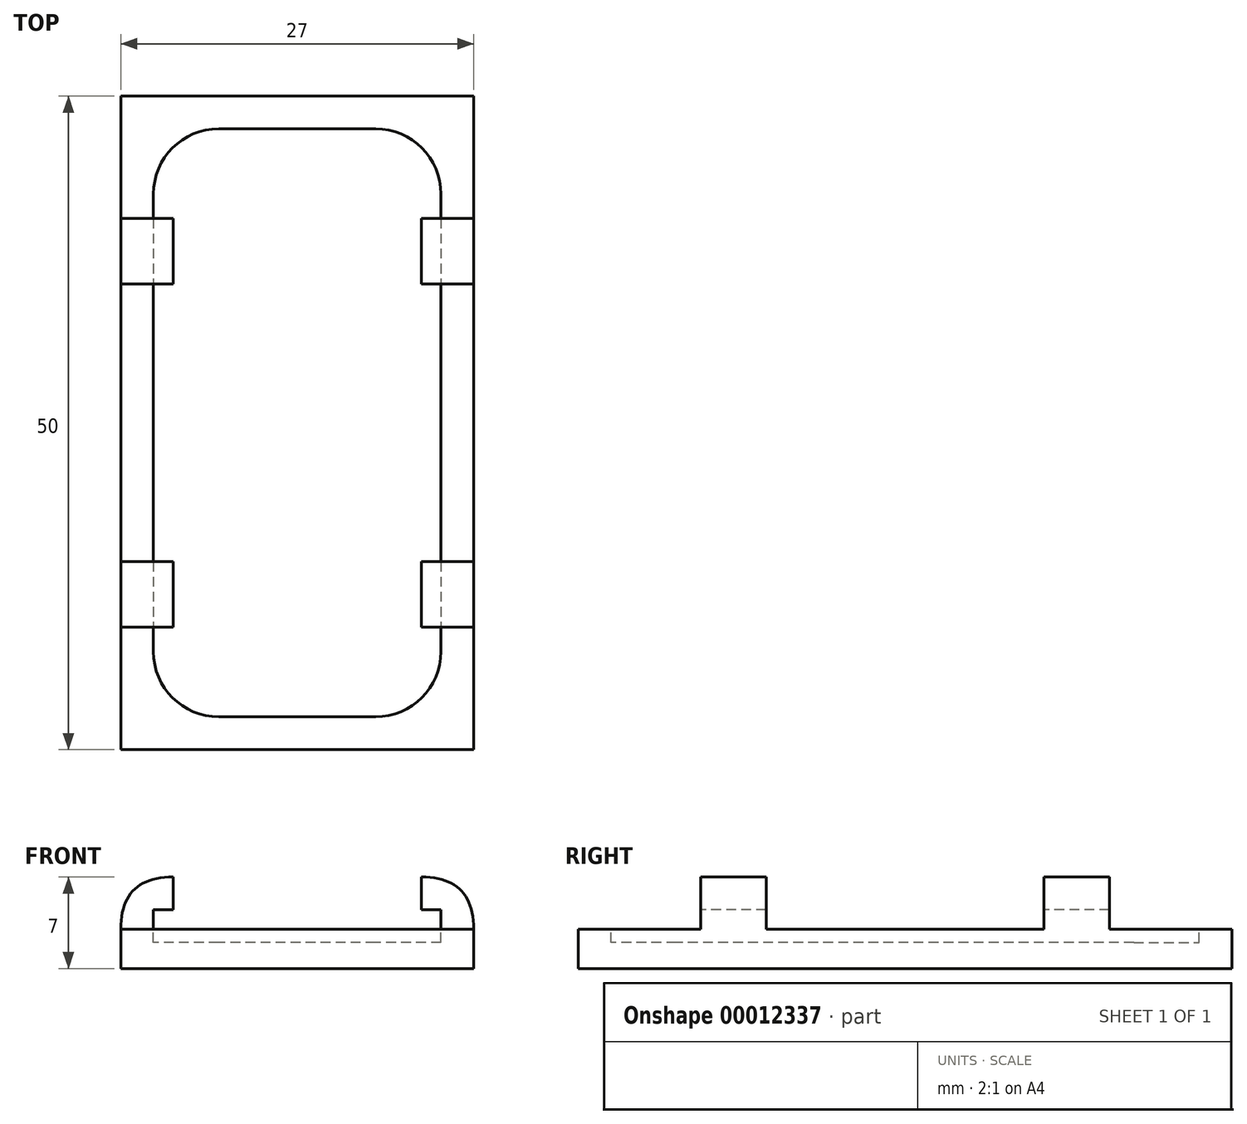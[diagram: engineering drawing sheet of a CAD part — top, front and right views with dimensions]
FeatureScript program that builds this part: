
annotation { "Feature Type Name" : "Feature", "Feature Type Description" : "" }
export const myFeature = defineFeature(function(context is Context, id is Id, definition is map)
    precondition{}
    {
        {
            var Q0;
            Q0=qCreatedBy(makeId("Top.planeOp"),FACE);
            var sketch = newSketch(context, id + "F0", { "sketchPlane" : qUnion([Q0])});
            skLineSegment(sketch, "E0.rect.bottom", {"start": v(13.5, 25) * mm, "end": v(-13.5, 25) * mm});
            skLineSegment(sketch, "E0.rect.top", {"start": v(13.5, -25) * mm, "end": v(-13.5, -25) * mm});
            skLineSegment(sketch, "E0.rect.left", {"start": v(13.5, 25) * mm, "end": v(13.5, -25) * mm});
            skLineSegment(sketch, "E0.rect.right", {"start": v(-13.5, 25) * mm, "end": v(-13.5, -25) * mm});
            skPoint(sketch, "E0.rect.middle", {"position": v(0, 0) * mm});
            skSolve(sketch);
        }
        {
            var Q0;
            Q0=qSketchRegion(id+"F0",true);
            extrude(context, id + "F1", {"entities" : qUnion([Q0]), "depth" : 3 * mm});
        }
        {
            var Q0;
            Q0=makeQuery(id+"F1.opExtrude","CAP_FACE",FACE,{"disambiguationData":[OSD([sQuery(id+"F0.wireOp",EDGE,"E0.rect.bottom"),sQuery(id+"F0.wireOp",EDGE,"E0.rect.top"),sQuery(id+"F0.wireOp",EDGE,"E0.rect.left"),sQuery(id+"F0.wireOp",EDGE,"E0.rect.right")])],"isStart":false});
            var sketch = newSketch(context, id + "F2", { "sketchPlane" : qUnion([Q0])});
            skLineSegment(sketch, "E1", {"start": v(-74.9, 0) * mm, "end": v(74.9, 0) * mm, "construction": true});
            skLineSegment(sketch, "E2", {"start": v(0, 55.47) * mm, "end": v(0, -72.68) * mm, "construction": true});
            skLineSegment(sketch, "E3.bottom", {"start": v(-13.5, 15.63) * mm, "end": v(-9.5, 15.63) * mm});
            skLineSegment(sketch, "E3.top", {"start": v(-13.5, 10.63) * mm, "end": v(-9.5, 10.63) * mm});
            skLineSegment(sketch, "E3.left", {"start": v(-13.5, 15.63) * mm, "end": v(-13.5, 10.63) * mm});
            skLineSegment(sketch, "E3.right", {"start": v(-9.5, 15.63) * mm, "end": v(-9.5, 10.63) * mm});
            skLineSegment(sketch, "E4.0.MirrorCS", {"start": v(13.5, 15.63) * mm, "end": v(9.5, 15.63) * mm});
            skLineSegment(sketch, "E5.0.MirrorCS", {"start": v(9.5, 15.63) * mm, "end": v(9.5, 10.63) * mm});
            skLineSegment(sketch, "E6.0.MirrorCS", {"start": v(13.5, 10.63) * mm, "end": v(9.5, 10.63) * mm});
            skLineSegment(sketch, "E7.0.MirrorCS", {"start": v(13.5, 15.63) * mm, "end": v(13.5, 10.63) * mm});
            skLineSegment(sketch, "E8.0.MirrorCS", {"start": v(-13.5, -10.63) * mm, "end": v(-9.5, -10.63) * mm});
            skLineSegment(sketch, "E9.0.MirrorCS", {"start": v(-9.5, -15.63) * mm, "end": v(-9.5, -10.63) * mm});
            skLineSegment(sketch, "E10.0.MirrorCS", {"start": v(-13.5, -15.63) * mm, "end": v(-9.5, -15.63) * mm});
            skLineSegment(sketch, "E11.0.MirrorCS", {"start": v(-13.5, -15.63) * mm, "end": v(-13.5, -10.63) * mm});
            skLineSegment(sketch, "E12.0.MirrorCS", {"start": v(13.5, -10.63) * mm, "end": v(9.5, -10.63) * mm});
            skLineSegment(sketch, "E13.0.MirrorCS", {"start": v(9.5, -15.63) * mm, "end": v(9.5, -10.63) * mm});
            skLineSegment(sketch, "E14.0.MirrorCS", {"start": v(13.5, -15.63) * mm, "end": v(9.5, -15.63) * mm});
            skLineSegment(sketch, "E15.0.MirrorCS", {"start": v(13.5, -15.63) * mm, "end": v(13.5, -10.63) * mm});
            skSolve(sketch);
        }
        {
            var Q0;
            Q0=makeQuery(id+"F2.imprint","IMPRINT",FACE,{"disambiguationData":[TD([[makeQuery(id+"F2.imprint","IMPRINT",EDGE,{"derivedFrom":makeQuery(id+"F1.opExtrude","CAP_EDGE",EDGE,{"disambiguationData":[OSD([sQuery(id+"F0.wireOp",EDGE,"E0.rect.bottom")])],"isStart":false})}),1.0]])]});
            var sketch = newSketch(context, id + "F3", { "sketchPlane" : qUnion([Q0])});
            skLineSegment(sketch, "E16.0", {"start": v(6, 22.5) * mm, "end": v(-6, 22.5) * mm});
            skLineSegment(sketch, "E16.1", {"start": v(11, 17.5) * mm, "end": v(11, -17.5) * mm});
            skLineSegment(sketch, "E16.2", {"start": v(6, -22.5) * mm, "end": v(-6, -22.5) * mm});
            skLineSegment(sketch, "E16.3", {"start": v(-11, 17.5) * mm, "end": v(-11, -17.5) * mm});
            skPoint(sketch, "E17.visualSharp", {"position": v(-11, 22.5) * mm});
            skArc(sketch, "E17.filletArc", {"start": v(-6, 22.5) * mm, "mid": v(-9.54, 21.04) * mm, "end": v(-11, 17.5) * mm});
            skPoint(sketch, "E18.visualSharp", {"position": v(11, 22.5) * mm});
            skArc(sketch, "E18.filletArc", {"start": v(11, 17.5) * mm, "mid": v(9.54, 21.04) * mm, "end": v(6, 22.5) * mm});
            skPoint(sketch, "E19.visualSharp", {"position": v(11, -22.5) * mm});
            skArc(sketch, "E19.filletArc", {"start": v(6, -22.5) * mm, "mid": v(9.54, -21.04) * mm, "end": v(11, -17.5) * mm});
            skPoint(sketch, "E20.visualSharp", {"position": v(-11, -22.5) * mm});
            skArc(sketch, "E20.filletArc", {"start": v(-11, -17.5) * mm, "mid": v(-9.54, -21.04) * mm, "end": v(-6, -22.5) * mm});
            skSolve(sketch);
        }
        {
            var Q0;
            Q0=qSketchRegion(id+"F3",true);
            extrude(context, id + "F4", {"entities" : qUnion([Q0]), "operationType" : NewBodyOperationType.REMOVE, "oppositeDirection" : true, "depth" : 1 * mm});
        }
        {
            var Q0;
            Q0=qSketchRegion(id+"F2",true);
            extrude(context, id + "F5", {"entities" : qUnion([Q0]), "operationType" : NewBodyOperationType.ADD, "depth" : 4 * mm});
        }
        {
            var Q0;
            Q0=makeQuery(id+"F5.opExtrude","SWEPT_FACE",FACE,{"disambiguationData":[OSD([sQuery(id+"F2.wireOp",EDGE,"E10.0.MirrorCS")])]});
            var sketch = newSketch(context, id + "F6", { "sketchPlane" : qUnion([Q0])});
            skLineSegment(sketch, "E21.bottom", {"start": v(-9.5, 4.5) * mm, "end": v(-11, 4.5) * mm});
            skLineSegment(sketch, "E21.top", {"start": v(-9.5, 3) * mm, "end": v(-11, 3) * mm});
            skLineSegment(sketch, "E21.left", {"start": v(-9.5, 4.5) * mm, "end": v(-9.5, 3) * mm});
            skLineSegment(sketch, "E21.right", {"start": v(-11, 4.5) * mm, "end": v(-11, 3) * mm});
            skLineSegment(sketch, "E22.0.MirrorCS", {"start": v(11, 4.5) * mm, "end": v(11, 3) * mm});
            skLineSegment(sketch, "E23.0.MirrorCS", {"start": v(9.5, 4.5) * mm, "end": v(11, 4.5) * mm});
            skLineSegment(sketch, "E24.0.MirrorCS", {"start": v(9.5, 4.5) * mm, "end": v(9.5, 3) * mm});
            skLineSegment(sketch, "E25.0.MirrorCS", {"start": v(9.5, 3) * mm, "end": v(11, 3) * mm});
            skSolve(sketch);
        }
        {
            var Q0;
            Q0=qSketchRegion(id+"F6",true);
            extrude(context, id + "F7", {"entities" : qUnion([Q0]), "operationType" : NewBodyOperationType.REMOVE, "endBound" : BoundingType.THROUGH_ALL, "oppositeDirection" : true, "depth" : 25 * mm});
        }
        {
            var Q0;
            Q0=makeQuery(id+"F5.opExtrude","CAP_EDGE",EDGE,{"disambiguationData":[OSD([sQuery(id+"F2.wireOp",EDGE,"E7.0.MirrorCS")])],"isStart":false});
            var Q1;
            Q1=makeQuery(id+"F5.opExtrude","CAP_EDGE",EDGE,{"disambiguationData":[OSD([sQuery(id+"F2.wireOp",EDGE,"E3.left")])],"isStart":false});
            var Q2;
            Q2=makeQuery(id+"F5.opExtrude","CAP_EDGE",EDGE,{"disambiguationData":[OSD([sQuery(id+"F2.wireOp",EDGE,"E11.0.MirrorCS")])],"isStart":false});
            var Q3;
            Q3=makeQuery(id+"F5.opExtrude","CAP_EDGE",EDGE,{"disambiguationData":[OSD([sQuery(id+"F2.wireOp",EDGE,"E15.0.MirrorCS")])],"isStart":false});
            fillet(context, id + "F8", {"entities" : qUnion([Q0, Q1, Q2, Q3]), "radius" : 4 * mm, "tangentPropagation" : true, "rho" : 0.5, "crossSection" : FilletCrossSection.CONIC, "allowEdgeOverflow" : false});
        }
    });
